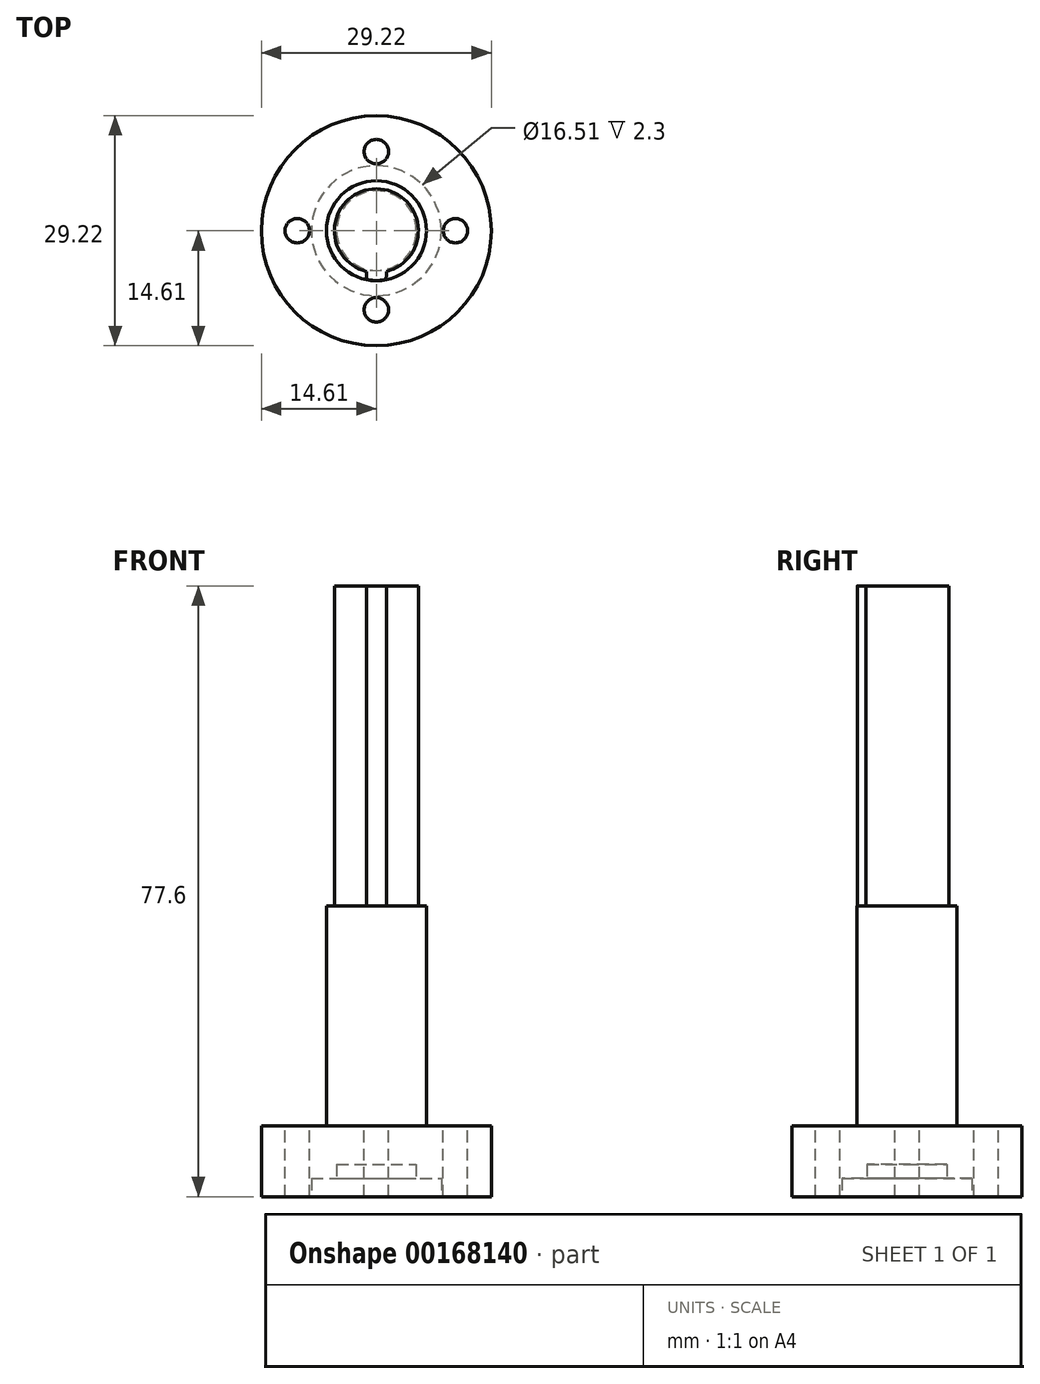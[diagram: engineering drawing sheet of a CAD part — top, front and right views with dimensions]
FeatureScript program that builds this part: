
annotation { "Feature Type Name" : "Feature", "Feature Type Description" : "" }
export const myFeature = defineFeature(function(context is Context, id is Id, definition is map)
    precondition{}
    {
        {
            var Q0;
            Q0=qCreatedBy(makeId("Top.planeOp"),FACE);
            var sketch = newSketch(context, id + "F0", { "sketchPlane" : qUnion([Q0])});
            skCircle(sketch, "E0", {"center": v(0, 0) * mm, "radius": 14.6 * mm});
            skSolve(sketch);
        }
        {
            var Q0;
            Q0=makeQuery(id+"F0.imprint","IMPRINT",FACE,{"disambiguationData":[TD([[makeQuery(id+"F0.imprint","IMPRINT",EDGE,{"derivedFrom":sQuery(id+"F0.wireOp",EDGE,"E0")}),1.0]])]});
            extrude(context, id + "F1", {"entities" : qUnion([Q0]), "depth" : 9.02 * mm});
        }
        {
            var Q0;
            Q0=makeQuery(id+"F1.opExtrude","CAP_FACE",FACE,{"disambiguationData":[OSD([sQuery(id+"F0.wireOp",EDGE,"E0")])],"isStart":false});
            var sketch = newSketch(context, id + "F2", { "sketchPlane" : qUnion([Q0])});
            skCircle(sketch, "E1", {"center": v(0, 0) * mm, "radius": 6.35 * mm});
            skSolve(sketch);
        }
        {
            var Q0;
            Q0=qSketchRegion(id+"F2",true);
            extrude(context, id + "F3", {"entities" : qUnion([Q0]), "operationType" : NewBodyOperationType.ADD, "depth" : 27.94 * mm});
        }
        {
            var Q0;
            Q0=makeQuery(id+"F3.opExtrude","CAP_FACE",FACE,{"disambiguationData":[OSD([sQuery(id+"F2.wireOp",EDGE,"E1")])],"isStart":false});
            var sketch = newSketch(context, id + "F4", { "sketchPlane" : qUnion([Q0])});
            skCircle(sketch, "E2", {"center": v(0, 0) * mm, "radius": 5.33 * mm});
            skSolve(sketch);
        }
        {
            var Q0;
            Q0=qSketchRegion(id+"F4",true);
            extrude(context, id + "F5", {"entities" : qUnion([Q0]), "operationType" : NewBodyOperationType.ADD, "depth" : 40.64 * mm});
        }
        {
            var Q0;
            Q0=makeQuery(id+"F1.opExtrude","CAP_FACE",FACE,{"disambiguationData":[OSD([sQuery(id+"F0.wireOp",EDGE,"E0")])],"isStart":true});
            var sketch = newSketch(context, id + "F6", { "sketchPlane" : qUnion([Q0])});
            skCircle(sketch, "E3", {"center": v(0, 0) * mm, "radius": 8.26 * mm});
            skSolve(sketch);
        }
        {
            var Q0;
            Q0=qSketchRegion(id+"F6",true);
            extrude(context, id + "F7", {"entities" : qUnion([Q0]), "operationType" : NewBodyOperationType.REMOVE, "oppositeDirection" : true, "depth" : 2.3 * mm});
        }
        {
            var Q0;
            Q0=makeQuery(id+"F1.opExtrude","CAP_FACE",FACE,{"disambiguationData":[OSD([sQuery(id+"F0.wireOp",EDGE,"E0")])],"isStart":true});
            var sketch = newSketch(context, id + "F8", { "sketchPlane" : qUnion([Q0])});
            skCircle(sketch, "E4", {"center": v(0, 0) * mm, "radius": 5.06 * mm});
            skSolve(sketch);
        }
        {
            var Q0;
            Q0=qSketchRegion(id+"F8",true);
            extrude(context, id + "F9", {"entities" : qUnion([Q0]), "operationType" : NewBodyOperationType.REMOVE, "oppositeDirection" : true, "depth" : 4.1 * mm});
        }
        {
            var Q0;
            Q0=makeQuery(id+"F1.opExtrude","CAP_FACE",FACE,{"disambiguationData":[OSD([sQuery(id+"F0.wireOp",EDGE,"E0")])],"isStart":false});
            var sketch = newSketch(context, id + "F10", { "sketchPlane" : qUnion([Q0])});
            skPoint(sketch, "E5", {"position": v(-10.05, 0) * mm});
            skPoint(sketch, "E6", {"position": v(0, 10.05) * mm});
            skPoint(sketch, "E7", {"position": v(10.05, 0) * mm});
            skPoint(sketch, "E8", {"position": v(0, -10.05) * mm});
            skCircle(sketch, "E9", {"center": v(0, 0) * mm, "radius": 10.05 * mm, "construction": true});
            skSolve(sketch);
        }
        {
            var Q0;
            Q0=sQuery(id+"F10.wireOp",VERTEX,"E8");
            var Q1;
            Q1=sQuery(id+"F10.wireOp",VERTEX,"E5");
            var Q2;
            Q2=sQuery(id+"F10.wireOp",VERTEX,"E6");
            var Q3;
            Q3=sQuery(id+"F10.wireOp",VERTEX,"E7");
            var Q4;
            Q4=makeQuery(id+"F1.opExtrude","SWEPT_BODY",BODY,{"disambiguationData":[OSD([sQuery(id+"F0.wireOp",EDGE,"E0")])]});
            hole(context, id + "F11", {"style" : HoleStyle.SIMPLE, "endStyle" : HoleEndStyle.THROUGH, "holeDiameter" : 3.1 * mm, "locations" : qUnion([Q0, Q1, Q2, Q3]), "scope" : qUnion([Q4]), "isTappedThrough" : true});
        }
        {
            var Q0;
            Q0=makeQuery(id+"F5.opExtrude","CAP_FACE",FACE,{"disambiguationData":[OSD([sQuery(id+"F4.wireOp",EDGE,"E2")])],"isStart":false});
            var sketch = newSketch(context, id + "F12", { "sketchPlane" : qUnion([Q0])});
            skArc(sketch, "E10", {"start": v(-1.27, -6.2) * mm, "mid": v(0, -6.32) * mm, "end": v(1.27, -6.2) * mm});
            skArc(sketch, "E11", {"start": v(-1.27, -5.18) * mm, "mid": v(0, -5.33) * mm, "end": v(1.27, -5.18) * mm});
            skLineSegment(sketch, "E12", {"start": v(-1.27, -6.2) * mm, "end": v(-1.27, -5.18) * mm});
            skLineSegment(sketch, "E13", {"start": v(1.27, -6.2) * mm, "end": v(1.27, -5.18) * mm});
            skSolve(sketch);
        }
        {
            var Q0;
            Q0=qSketchRegion(id+"F12",true);
            var Q1;
            Q1=makeQuery(id+"F3.opExtrude","CAP_FACE",FACE,{"disambiguationData":[OSD([sQuery(id+"F2.wireOp",EDGE,"E1")])],"isStart":false});
            extrude(context, id + "F13", {"entities" : qUnion([Q0]), "operationType" : NewBodyOperationType.ADD, "endBound" : BoundingType.UP_TO_SURFACE, "oppositeDirection" : true, "endBoundEntityFace" : qUnion([Q1]), "depth" : 25.4 * mm});
        }
        {
            var Q0;
            Q0=makeQuery(id+"F13.opExtrude","SWEPT_EDGE",EDGE,{"disambiguationData":[OSD([sQuery(id+"F12.wireOp",EDGE,"E10"),sQuery(id+"F12.wireOp",EDGE,"E13")])]});
            var Q1;
            Q1=makeQuery(id+"F13.opExtrude","SWEPT_EDGE",EDGE,{"disambiguationData":[OSD([sQuery(id+"F4.wireOp",EDGE,"E2"),sQuery(id+"F12.wireOp",EDGE,"E11"),sQuery(id+"F12.wireOp",EDGE,"E13")])]});
            var Q2;
            Q2=makeQuery(id+"F13.opExtrude","SWEPT_EDGE",EDGE,{"disambiguationData":[OSD([sQuery(id+"F12.wireOp",EDGE,"E10"),sQuery(id+"F12.wireOp",EDGE,"E12")])]});
            var Q3;
            Q3=makeQuery(id+"F13.opExtrude","SWEPT_EDGE",EDGE,{"disambiguationData":[OSD([sQuery(id+"F4.wireOp",EDGE,"E2"),sQuery(id+"F12.wireOp",EDGE,"E11"),sQuery(id+"F12.wireOp",EDGE,"E12")])]});
            fillet(context, id + "F14", {"entities" : qUnion([Q0, Q1, Q2, Q3]), "radius" : 0.5 * mm, "tangentPropagation" : true, "allowEdgeOverflow" : false});
        }
    });
